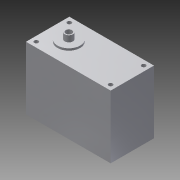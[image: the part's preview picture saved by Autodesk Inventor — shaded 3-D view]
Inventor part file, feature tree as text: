
AUTODESK INVENTOR PART (.ipt)
format: ipt  version: 2015 (Build 190159000, 159)  size: 157,184 bytes
history: native  units: mm
features: sketch x9, extrude x8, other x1, hole x1
ambient origin geometry x8: Origin, YZ Plane, XZ Plane, XY Plane, X Axis, Y Axis, Z Axis, Center Point
bodies: Body1 (feature_tree)
feature tree (19):
  other  "ソリッド1"
  extrude  "押し出し1"  Depth=41.0mm
  hole  "穴1"  [1 undecoded]
  extrude  "押し出し2"  Depth=30.5mm TaperAngle=0.0deg
  extrude  "押し出し3"  Depth=11.0mm
  extrude  "押し出し4"  Depth=1.0mm TaperAngle=0.0deg
  extrude  "押し出し5"  Depth=3.0mm
  extrude  "押し出し6"  Depth=40.0mm TaperAngle=0.0deg
  extrude  "押し出し7"  Depth=4.0mm
  extrude  "押し出し8"  Depth=3.0mm TaperAngle=0.0deg
  sketch  "スケッチ1"
  sketch  "スケッチ2"
  sketch  "スケッチ3"
  sketch  "スケッチ4"
  sketch  "スケッチ5"
  sketch  "スケッチ6"
  sketch  "スケッチ8"
  sketch  "スケッチ9"
  sketch  "スケッチ10"
note: 1 required parameter value undecoded (feature->parameter linkage not recoverable at this tier; creation-order binding heuristic only, values carry confidence <= 0.55)
